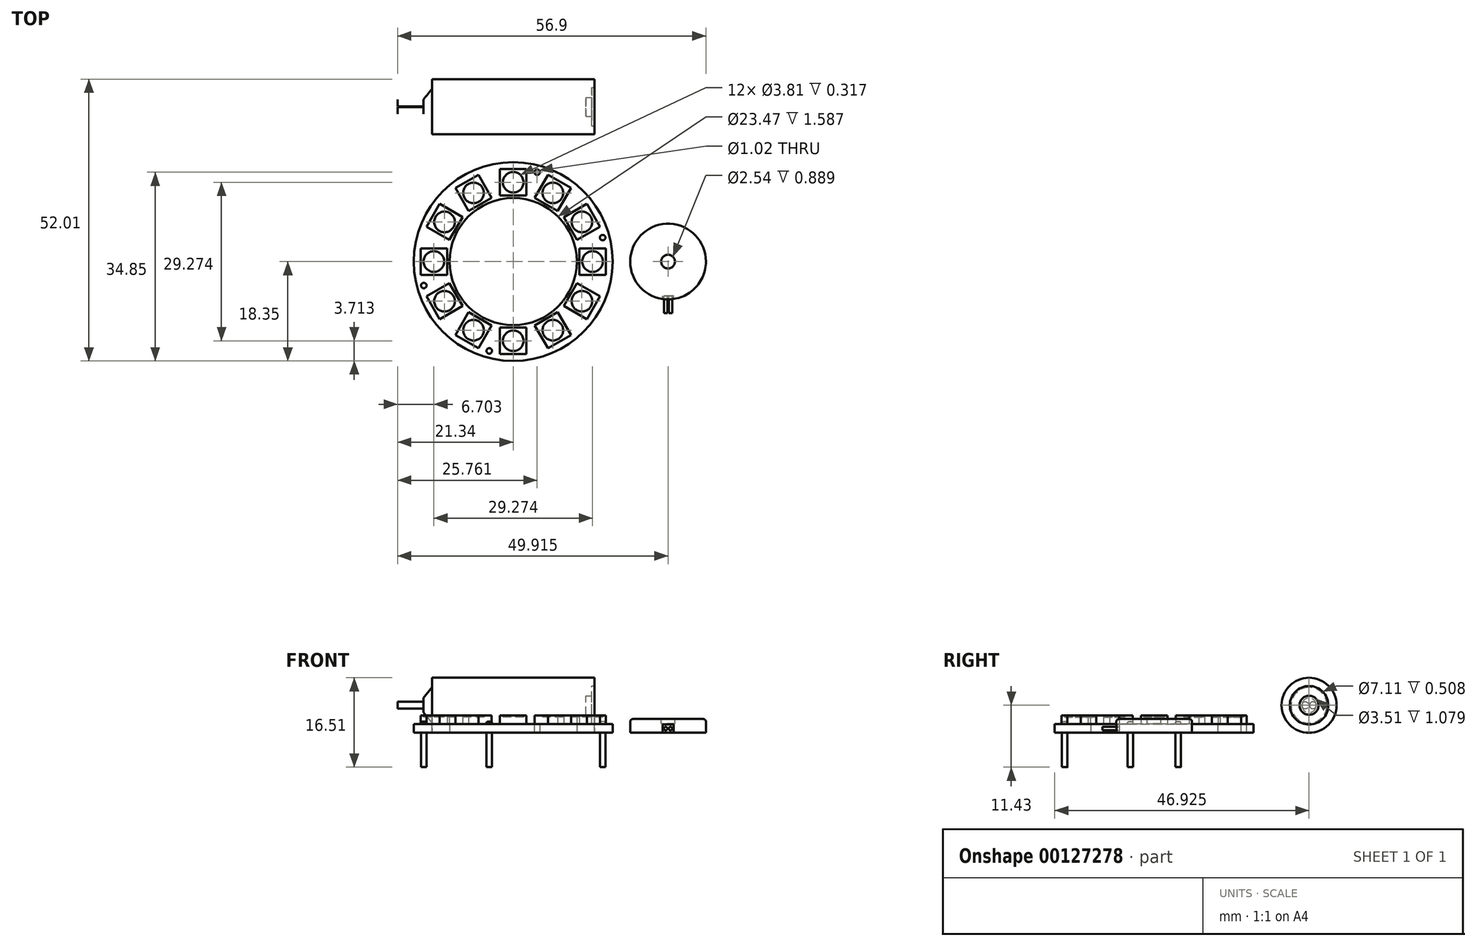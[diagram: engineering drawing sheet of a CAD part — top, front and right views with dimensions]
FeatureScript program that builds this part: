
annotation { "Feature Type Name" : "Feature", "Feature Type Description" : "" }
export const myFeature = defineFeature(function(context is Context, id is Id, definition is map)
    precondition{}
    {
        {
            var Q0;
            Q0=qCreatedBy(makeId("Top.planeOp"),FACE);
            var sketch = newSketch(context, id + "F0", { "sketchPlane" : qUnion([Q0])});
            skCircle(sketch, "E0", {"center": v(0, 0) * mm, "radius": 18.35 * mm});
            skCircle(sketch, "E1", {"center": v(0, 0) * mm, "radius": 11.73 * mm});
            skLineSegment(sketch, "E2", {"start": v(0, 0) * mm, "end": v(0, 18.35) * mm, "construction": true});
            skLineSegment(sketch, "E3.1.0", {"start": v(0, 0) * mm, "end": v(-4.75, 17.73) * mm, "construction": true});
            skLineSegment(sketch, "E3.2.0", {"start": v(0, 0) * mm, "end": v(-9.18, 15.9) * mm, "construction": true});
            skLineSegment(sketch, "E3.3.0", {"start": v(0, 0) * mm, "end": v(-12.98, 12.98) * mm, "construction": true});
            skLineSegment(sketch, "E3.4.0", {"start": v(0, 0) * mm, "end": v(-15.9, 9.18) * mm, "construction": true});
            skLineSegment(sketch, "E3.5.0", {"start": v(0, 0) * mm, "end": v(-17.73, 4.75) * mm, "construction": true});
            skLineSegment(sketch, "E3.6.0", {"start": v(0, 0) * mm, "end": v(-18.35, 0) * mm, "construction": true});
            skLineSegment(sketch, "E3.7.0", {"start": v(0, 0) * mm, "end": v(-17.73, -4.75) * mm, "construction": true});
            skLineSegment(sketch, "E3.8.0", {"start": v(0, 0) * mm, "end": v(-15.9, -9.18) * mm, "construction": true});
            skLineSegment(sketch, "E3.9.0", {"start": v(0, 0) * mm, "end": v(-12.98, -12.98) * mm, "construction": true});
            skLineSegment(sketch, "E3.10.0", {"start": v(0, 0) * mm, "end": v(-9.18, -15.9) * mm, "construction": true});
            skLineSegment(sketch, "E3.11.0", {"start": v(0, 0) * mm, "end": v(-4.75, -17.73) * mm, "construction": true});
            skLineSegment(sketch, "E3.12.0", {"start": v(0, 0) * mm, "end": v(0, -18.35) * mm, "construction": true});
            skLineSegment(sketch, "E3.13.0", {"start": v(0, 0) * mm, "end": v(4.75, -17.73) * mm, "construction": true});
            skLineSegment(sketch, "E3.14.0", {"start": v(0, 0) * mm, "end": v(9.18, -15.9) * mm, "construction": true});
            skLineSegment(sketch, "E3.15.0", {"start": v(0, 0) * mm, "end": v(12.98, -12.98) * mm, "construction": true});
            skLineSegment(sketch, "E3.16.0", {"start": v(0, 0) * mm, "end": v(15.9, -9.18) * mm, "construction": true});
            skLineSegment(sketch, "E3.17.0", {"start": v(0, 0) * mm, "end": v(17.73, -4.75) * mm, "construction": true});
            skLineSegment(sketch, "E3.18.0", {"start": v(0, 0) * mm, "end": v(18.35, 0) * mm, "construction": true});
            skLineSegment(sketch, "E3.19.0", {"start": v(0, 0) * mm, "end": v(17.73, 4.75) * mm, "construction": true});
            skLineSegment(sketch, "E3.20.0", {"start": v(0, 0) * mm, "end": v(15.9, 9.18) * mm, "construction": true});
            skLineSegment(sketch, "E3.21.0", {"start": v(0, 0) * mm, "end": v(12.98, 12.98) * mm, "construction": true});
            skLineSegment(sketch, "E3.22.0", {"start": v(0, 0) * mm, "end": v(9.18, 15.9) * mm, "construction": true});
            skLineSegment(sketch, "E3.23.0", {"start": v(0, 0) * mm, "end": v(4.75, 17.73) * mm, "construction": true});
            skCircle(sketch, "E4", {"center": v(4.42, 16.5) * mm, "radius": 0.5 * mm});
            skCircle(sketch, "E5", {"center": v(16.5, 4.42) * mm, "radius": 0.5 * mm});
            skCircle(sketch, "E6", {"center": v(-16.5, -4.42) * mm, "radius": 0.5 * mm});
            skCircle(sketch, "E7", {"center": v(-4.42, -16.5) * mm, "radius": 0.5 * mm});
            skSolve(sketch);
        }
        {
            var Q0;
            Q0=makeQuery(id+"F0.imprint","IMPRINT",FACE,{"disambiguationData":[TD([[makeQuery(id+"F0.imprint","IMPRINT",EDGE,{"derivedFrom":sQuery(id+"F0.wireOp",EDGE,"E0")}),1.0]])]});
            extrude(context, id + "F1", {"entities" : qUnion([Q0]), "depth" : 1.59 * mm});
        }
        {
            var Q0;
            Q0=makeQuery(id+"F1.opExtrude","CAP_FACE",FACE,{"disambiguationData":[OSD([sQuery(id+"F0.wireOp",EDGE,"E0"),sQuery(id+"F0.wireOp",EDGE,"E1"),sQuery(id+"F0.wireOp",EDGE,"E4"),sQuery(id+"F0.wireOp",EDGE,"E5"),sQuery(id+"F0.wireOp",EDGE,"E6"),sQuery(id+"F0.wireOp",EDGE,"E7")])],"isStart":false});
            var sketch = newSketch(context, id + "F2", { "sketchPlane" : qUnion([Q0])});
            skLineSegment(sketch, "E8.bottom", {"start": v(-2.44, 17.08) * mm, "end": v(2.44, 17.08) * mm});
            skLineSegment(sketch, "E8.top", {"start": v(-2.44, 12.2) * mm, "end": v(2.44, 12.2) * mm});
            skLineSegment(sketch, "E8.left", {"start": v(-2.44, 17.08) * mm, "end": v(-2.44, 12.2) * mm});
            skLineSegment(sketch, "E8.right", {"start": v(2.44, 17.08) * mm, "end": v(2.44, 12.2) * mm});
            skCircle(sketch, "E9", {"center": v(0, 14.64) * mm, "radius": 1.9 * mm});
            skPoint(sketch, "E9.centerSnap0", {"position": v(-2.44, 14.64) * mm});
            skCircle(sketch, "E10.1.0", {"center": v(-7.32, 12.68) * mm, "radius": 1.9 * mm});
            skLineSegment(sketch, "E10.1.1", {"start": v(-10.66, 13.57) * mm, "end": v(-6.42, 16.02) * mm});
            skLineSegment(sketch, "E10.1.2", {"start": v(-6.42, 16.02) * mm, "end": v(-3.98, 11.78) * mm});
            skLineSegment(sketch, "E10.1.3", {"start": v(-8.21, 9.34) * mm, "end": v(-3.98, 11.78) * mm});
            skLineSegment(sketch, "E10.1.4", {"start": v(-10.66, 13.57) * mm, "end": v(-8.21, 9.34) * mm});
            skCircle(sketch, "E10.2.0", {"center": v(-12.68, 7.32) * mm, "radius": 1.9 * mm});
            skLineSegment(sketch, "E10.2.1", {"start": v(-16.02, 6.42) * mm, "end": v(-13.57, 10.66) * mm});
            skLineSegment(sketch, "E10.2.2", {"start": v(-13.57, 10.66) * mm, "end": v(-9.34, 8.21) * mm});
            skLineSegment(sketch, "E10.2.3", {"start": v(-11.78, 3.98) * mm, "end": v(-9.34, 8.21) * mm});
            skLineSegment(sketch, "E10.2.4", {"start": v(-16.02, 6.42) * mm, "end": v(-11.78, 3.98) * mm});
            skCircle(sketch, "E10.3.0", {"center": v(-14.64, 0) * mm, "radius": 1.9 * mm});
            skLineSegment(sketch, "E10.3.1", {"start": v(-17.08, -2.44) * mm, "end": v(-17.08, 2.44) * mm});
            skLineSegment(sketch, "E10.3.2", {"start": v(-17.08, 2.44) * mm, "end": v(-12.2, 2.44) * mm});
            skLineSegment(sketch, "E10.3.3", {"start": v(-12.2, -2.44) * mm, "end": v(-12.2, 2.44) * mm});
            skLineSegment(sketch, "E10.3.4", {"start": v(-17.08, -2.44) * mm, "end": v(-12.2, -2.44) * mm});
            skCircle(sketch, "E10.4.0", {"center": v(-12.68, -7.32) * mm, "radius": 1.9 * mm});
            skLineSegment(sketch, "E10.4.1", {"start": v(-13.57, -10.66) * mm, "end": v(-16.02, -6.42) * mm});
            skLineSegment(sketch, "E10.4.2", {"start": v(-16.02, -6.42) * mm, "end": v(-11.78, -3.98) * mm});
            skLineSegment(sketch, "E10.4.3", {"start": v(-9.34, -8.21) * mm, "end": v(-11.78, -3.98) * mm});
            skLineSegment(sketch, "E10.4.4", {"start": v(-13.57, -10.66) * mm, "end": v(-9.34, -8.21) * mm});
            skCircle(sketch, "E10.5.0", {"center": v(-7.32, -12.68) * mm, "radius": 1.9 * mm});
            skLineSegment(sketch, "E10.5.1", {"start": v(-6.42, -16.02) * mm, "end": v(-10.66, -13.57) * mm});
            skLineSegment(sketch, "E10.5.2", {"start": v(-10.66, -13.57) * mm, "end": v(-8.21, -9.34) * mm});
            skLineSegment(sketch, "E10.5.3", {"start": v(-3.98, -11.78) * mm, "end": v(-8.21, -9.34) * mm});
            skLineSegment(sketch, "E10.5.4", {"start": v(-6.42, -16.02) * mm, "end": v(-3.98, -11.78) * mm});
            skCircle(sketch, "E10.6.0", {"center": v(0, -14.64) * mm, "radius": 1.9 * mm});
            skLineSegment(sketch, "E10.6.1", {"start": v(2.44, -17.08) * mm, "end": v(-2.44, -17.08) * mm});
            skLineSegment(sketch, "E10.6.2", {"start": v(-2.44, -17.08) * mm, "end": v(-2.44, -12.2) * mm});
            skLineSegment(sketch, "E10.6.3", {"start": v(2.44, -12.2) * mm, "end": v(-2.44, -12.2) * mm});
            skLineSegment(sketch, "E10.6.4", {"start": v(2.44, -17.08) * mm, "end": v(2.44, -12.2) * mm});
            skCircle(sketch, "E10.7.0", {"center": v(7.32, -12.68) * mm, "radius": 1.9 * mm});
            skLineSegment(sketch, "E10.7.1", {"start": v(10.66, -13.57) * mm, "end": v(6.42, -16.02) * mm});
            skLineSegment(sketch, "E10.7.2", {"start": v(6.42, -16.02) * mm, "end": v(3.98, -11.78) * mm});
            skLineSegment(sketch, "E10.7.3", {"start": v(8.21, -9.34) * mm, "end": v(3.98, -11.78) * mm});
            skLineSegment(sketch, "E10.7.4", {"start": v(10.66, -13.57) * mm, "end": v(8.21, -9.34) * mm});
            skCircle(sketch, "E10.8.0", {"center": v(12.68, -7.32) * mm, "radius": 1.9 * mm});
            skLineSegment(sketch, "E10.8.1", {"start": v(16.02, -6.42) * mm, "end": v(13.57, -10.66) * mm});
            skLineSegment(sketch, "E10.8.2", {"start": v(13.57, -10.66) * mm, "end": v(9.34, -8.21) * mm});
            skLineSegment(sketch, "E10.8.3", {"start": v(11.78, -3.98) * mm, "end": v(9.34, -8.21) * mm});
            skLineSegment(sketch, "E10.8.4", {"start": v(16.02, -6.42) * mm, "end": v(11.78, -3.98) * mm});
            skCircle(sketch, "E10.9.0", {"center": v(14.64, 0) * mm, "radius": 1.9 * mm});
            skLineSegment(sketch, "E10.9.1", {"start": v(17.08, 2.44) * mm, "end": v(17.08, -2.44) * mm});
            skLineSegment(sketch, "E10.9.2", {"start": v(17.08, -2.44) * mm, "end": v(12.2, -2.44) * mm});
            skLineSegment(sketch, "E10.9.3", {"start": v(12.2, 2.44) * mm, "end": v(12.2, -2.44) * mm});
            skLineSegment(sketch, "E10.9.4", {"start": v(17.08, 2.44) * mm, "end": v(12.2, 2.44) * mm});
            skCircle(sketch, "E10.10.0", {"center": v(12.68, 7.32) * mm, "radius": 1.9 * mm});
            skLineSegment(sketch, "E10.10.1", {"start": v(13.57, 10.66) * mm, "end": v(16.02, 6.42) * mm});
            skLineSegment(sketch, "E10.10.2", {"start": v(16.02, 6.42) * mm, "end": v(11.78, 3.98) * mm});
            skLineSegment(sketch, "E10.10.3", {"start": v(9.34, 8.21) * mm, "end": v(11.78, 3.98) * mm});
            skLineSegment(sketch, "E10.10.4", {"start": v(13.57, 10.66) * mm, "end": v(9.34, 8.21) * mm});
            skCircle(sketch, "E10.11.0", {"center": v(7.32, 12.68) * mm, "radius": 1.9 * mm});
            skLineSegment(sketch, "E10.11.1", {"start": v(6.42, 16.02) * mm, "end": v(10.66, 13.57) * mm});
            skLineSegment(sketch, "E10.11.2", {"start": v(10.66, 13.57) * mm, "end": v(8.21, 9.34) * mm});
            skLineSegment(sketch, "E10.11.3", {"start": v(3.98, 11.78) * mm, "end": v(8.21, 9.34) * mm});
            skLineSegment(sketch, "E10.11.4", {"start": v(6.42, 16.02) * mm, "end": v(3.98, 11.78) * mm});
            skPoint(sketch, "E10.center", {"position": v(0, 0) * mm});
            skSolve(sketch);
        }
        {
            var Q0;
            Q0=qSketchRegion(id+"F2",true);
            extrude(context, id + "F3", {"entities" : qUnion([Q0]), "operationType" : NewBodyOperationType.ADD, "depth" : 1.59 * mm});
        }
        {
            var Q0;
            Q0=makeQuery(id+"F3.boolean.opBoolean","SPLIT",FACE,{"disambiguationData":[TD([makeQuery(id+"F3.opExtrude","SWEPT_FACE",FACE,{"disambiguationData":[OSD([sQuery(id+"F2.wireOp",EDGE,"E9")])]})])],"derivedFrom":makeQuery(id+"F1.opExtrude","CAP_FACE",FACE,{"disambiguationData":[OSD([sQuery(id+"F0.wireOp",EDGE,"E0"),sQuery(id+"F0.wireOp",EDGE,"E1"),sQuery(id+"F0.wireOp",EDGE,"E4"),sQuery(id+"F0.wireOp",EDGE,"E5"),sQuery(id+"F0.wireOp",EDGE,"E6"),sQuery(id+"F0.wireOp",EDGE,"E7")])],"isStart":false})});
            var Q1;
            Q1=makeQuery(id+"F3.boolean.opBoolean","SPLIT",FACE,{"disambiguationData":[TD([makeQuery(id+"F3.opExtrude","SWEPT_FACE",FACE,{"disambiguationData":[OSD([sQuery(id+"F2.wireOp",EDGE,"E10.11.0")])]})])],"derivedFrom":makeQuery(id+"F1.opExtrude","CAP_FACE",FACE,{"disambiguationData":[OSD([sQuery(id+"F0.wireOp",EDGE,"E0"),sQuery(id+"F0.wireOp",EDGE,"E1"),sQuery(id+"F0.wireOp",EDGE,"E4"),sQuery(id+"F0.wireOp",EDGE,"E5"),sQuery(id+"F0.wireOp",EDGE,"E6"),sQuery(id+"F0.wireOp",EDGE,"E7")])],"isStart":false})});
            var Q2;
            Q2=makeQuery(id+"F3.boolean.opBoolean","SPLIT",FACE,{"disambiguationData":[TD([makeQuery(id+"F3.opExtrude","SWEPT_FACE",FACE,{"disambiguationData":[OSD([sQuery(id+"F2.wireOp",EDGE,"E10.10.0")])]})])],"derivedFrom":makeQuery(id+"F1.opExtrude","CAP_FACE",FACE,{"disambiguationData":[OSD([sQuery(id+"F0.wireOp",EDGE,"E0"),sQuery(id+"F0.wireOp",EDGE,"E1"),sQuery(id+"F0.wireOp",EDGE,"E4"),sQuery(id+"F0.wireOp",EDGE,"E5"),sQuery(id+"F0.wireOp",EDGE,"E6"),sQuery(id+"F0.wireOp",EDGE,"E7")])],"isStart":false})});
            var Q3;
            Q3=makeQuery(id+"F3.boolean.opBoolean","SPLIT",FACE,{"disambiguationData":[TD([makeQuery(id+"F3.opExtrude","SWEPT_FACE",FACE,{"disambiguationData":[OSD([sQuery(id+"F2.wireOp",EDGE,"E10.9.0")])]})])],"derivedFrom":makeQuery(id+"F1.opExtrude","CAP_FACE",FACE,{"disambiguationData":[OSD([sQuery(id+"F0.wireOp",EDGE,"E0"),sQuery(id+"F0.wireOp",EDGE,"E1"),sQuery(id+"F0.wireOp",EDGE,"E4"),sQuery(id+"F0.wireOp",EDGE,"E5"),sQuery(id+"F0.wireOp",EDGE,"E6"),sQuery(id+"F0.wireOp",EDGE,"E7")])],"isStart":false})});
            var Q4;
            Q4=makeQuery(id+"F3.boolean.opBoolean","SPLIT",FACE,{"disambiguationData":[TD([makeQuery(id+"F3.opExtrude","SWEPT_FACE",FACE,{"disambiguationData":[OSD([sQuery(id+"F2.wireOp",EDGE,"E10.8.0")])]})])],"derivedFrom":makeQuery(id+"F1.opExtrude","CAP_FACE",FACE,{"disambiguationData":[OSD([sQuery(id+"F0.wireOp",EDGE,"E0"),sQuery(id+"F0.wireOp",EDGE,"E1"),sQuery(id+"F0.wireOp",EDGE,"E4"),sQuery(id+"F0.wireOp",EDGE,"E5"),sQuery(id+"F0.wireOp",EDGE,"E6"),sQuery(id+"F0.wireOp",EDGE,"E7")])],"isStart":false})});
            var Q5;
            Q5=makeQuery(id+"F3.boolean.opBoolean","SPLIT",FACE,{"disambiguationData":[TD([makeQuery(id+"F3.opExtrude","SWEPT_FACE",FACE,{"disambiguationData":[OSD([sQuery(id+"F2.wireOp",EDGE,"E10.7.0")])]})])],"derivedFrom":makeQuery(id+"F1.opExtrude","CAP_FACE",FACE,{"disambiguationData":[OSD([sQuery(id+"F0.wireOp",EDGE,"E0"),sQuery(id+"F0.wireOp",EDGE,"E1"),sQuery(id+"F0.wireOp",EDGE,"E4"),sQuery(id+"F0.wireOp",EDGE,"E5"),sQuery(id+"F0.wireOp",EDGE,"E6"),sQuery(id+"F0.wireOp",EDGE,"E7")])],"isStart":false})});
            var Q6;
            Q6=makeQuery(id+"F3.boolean.opBoolean","SPLIT",FACE,{"disambiguationData":[TD([makeQuery(id+"F3.opExtrude","SWEPT_FACE",FACE,{"disambiguationData":[OSD([sQuery(id+"F2.wireOp",EDGE,"E10.6.0")])]})])],"derivedFrom":makeQuery(id+"F1.opExtrude","CAP_FACE",FACE,{"disambiguationData":[OSD([sQuery(id+"F0.wireOp",EDGE,"E0"),sQuery(id+"F0.wireOp",EDGE,"E1"),sQuery(id+"F0.wireOp",EDGE,"E4"),sQuery(id+"F0.wireOp",EDGE,"E5"),sQuery(id+"F0.wireOp",EDGE,"E6"),sQuery(id+"F0.wireOp",EDGE,"E7")])],"isStart":false})});
            var Q7;
            Q7=makeQuery(id+"F3.boolean.opBoolean","SPLIT",FACE,{"disambiguationData":[TD([makeQuery(id+"F3.opExtrude","SWEPT_FACE",FACE,{"disambiguationData":[OSD([sQuery(id+"F2.wireOp",EDGE,"E10.5.0")])]})])],"derivedFrom":makeQuery(id+"F1.opExtrude","CAP_FACE",FACE,{"disambiguationData":[OSD([sQuery(id+"F0.wireOp",EDGE,"E0"),sQuery(id+"F0.wireOp",EDGE,"E1"),sQuery(id+"F0.wireOp",EDGE,"E4"),sQuery(id+"F0.wireOp",EDGE,"E5"),sQuery(id+"F0.wireOp",EDGE,"E6"),sQuery(id+"F0.wireOp",EDGE,"E7")])],"isStart":false})});
            var Q8;
            Q8=makeQuery(id+"F3.boolean.opBoolean","SPLIT",FACE,{"disambiguationData":[TD([makeQuery(id+"F3.opExtrude","SWEPT_FACE",FACE,{"disambiguationData":[OSD([sQuery(id+"F2.wireOp",EDGE,"E10.4.0")])]})])],"derivedFrom":makeQuery(id+"F1.opExtrude","CAP_FACE",FACE,{"disambiguationData":[OSD([sQuery(id+"F0.wireOp",EDGE,"E0"),sQuery(id+"F0.wireOp",EDGE,"E1"),sQuery(id+"F0.wireOp",EDGE,"E4"),sQuery(id+"F0.wireOp",EDGE,"E5"),sQuery(id+"F0.wireOp",EDGE,"E6"),sQuery(id+"F0.wireOp",EDGE,"E7")])],"isStart":false})});
            var Q9;
            Q9=makeQuery(id+"F3.boolean.opBoolean","SPLIT",FACE,{"disambiguationData":[TD([makeQuery(id+"F3.opExtrude","SWEPT_FACE",FACE,{"disambiguationData":[OSD([sQuery(id+"F2.wireOp",EDGE,"E10.3.0")])]})])],"derivedFrom":makeQuery(id+"F1.opExtrude","CAP_FACE",FACE,{"disambiguationData":[OSD([sQuery(id+"F0.wireOp",EDGE,"E0"),sQuery(id+"F0.wireOp",EDGE,"E1"),sQuery(id+"F0.wireOp",EDGE,"E4"),sQuery(id+"F0.wireOp",EDGE,"E5"),sQuery(id+"F0.wireOp",EDGE,"E6"),sQuery(id+"F0.wireOp",EDGE,"E7")])],"isStart":false})});
            var Q10;
            Q10=makeQuery(id+"F3.boolean.opBoolean","SPLIT",FACE,{"disambiguationData":[TD([makeQuery(id+"F3.opExtrude","SWEPT_FACE",FACE,{"disambiguationData":[OSD([sQuery(id+"F2.wireOp",EDGE,"E10.2.0")])]})])],"derivedFrom":makeQuery(id+"F1.opExtrude","CAP_FACE",FACE,{"disambiguationData":[OSD([sQuery(id+"F0.wireOp",EDGE,"E0"),sQuery(id+"F0.wireOp",EDGE,"E1"),sQuery(id+"F0.wireOp",EDGE,"E4"),sQuery(id+"F0.wireOp",EDGE,"E5"),sQuery(id+"F0.wireOp",EDGE,"E6"),sQuery(id+"F0.wireOp",EDGE,"E7")])],"isStart":false})});
            var Q11;
            Q11=makeQuery(id+"F3.boolean.opBoolean","SPLIT",FACE,{"disambiguationData":[TD([makeQuery(id+"F3.opExtrude","SWEPT_FACE",FACE,{"disambiguationData":[OSD([sQuery(id+"F2.wireOp",EDGE,"E10.1.0")])]})])],"derivedFrom":makeQuery(id+"F1.opExtrude","CAP_FACE",FACE,{"disambiguationData":[OSD([sQuery(id+"F0.wireOp",EDGE,"E0"),sQuery(id+"F0.wireOp",EDGE,"E1"),sQuery(id+"F0.wireOp",EDGE,"E4"),sQuery(id+"F0.wireOp",EDGE,"E5"),sQuery(id+"F0.wireOp",EDGE,"E6"),sQuery(id+"F0.wireOp",EDGE,"E7")])],"isStart":false})});
            extrude(context, id + "F4", {"entities" : qUnion([Q0, Q1, Q2, Q3, Q4, Q5, Q6, Q7, Q8, Q9, Q10, Q11]), "operationType" : NewBodyOperationType.ADD, "depth" : 1.27 * mm});
        }
        {
            var Q0;
            Q0=makeQuery(id+"F0.imprint","IMPRINT",FACE,{"disambiguationData":[TD([[makeQuery(id+"F0.imprint","IMPRINT",EDGE,{"derivedFrom":sQuery(id+"F0.wireOp",EDGE,"E7")}),1.0]])]});
            var Q1;
            Q1=makeQuery(id+"F0.imprint","IMPRINT",FACE,{"disambiguationData":[TD([[makeQuery(id+"F0.imprint","IMPRINT",EDGE,{"derivedFrom":sQuery(id+"F0.wireOp",EDGE,"E6")}),1.0]])]});
            var Q2;
            Q2=makeQuery(id+"F0.imprint","IMPRINT",FACE,{"disambiguationData":[TD([[makeQuery(id+"F0.imprint","IMPRINT",EDGE,{"derivedFrom":sQuery(id+"F0.wireOp",EDGE,"E5")}),1.0]])]});
            extrude(context, id + "F5", {"entities" : qUnion([Q0, Q1, Q2]), "operationType" : NewBodyOperationType.ADD, "oppositeDirection" : true, "depth" : 6.35 * mm, "hasSecondDirection" : true, "secondDirectionOppositeDirection" : false, "secondDirectionDepth" : 2.03 * mm});
        }
        {
            var Q0;
            Q0=makeQuery(id+"F1.opExtrude","CAP_EDGE",EDGE,{"disambiguationData":[OSD([sQuery(id+"F0.wireOp",EDGE,"E5")])],"isStart":false});
            var Q1;
            Q1=makeQuery(id+"F5.opExtrude","CAP_EDGE",EDGE,{"disambiguationData":[OSD([sQuery(id+"F0.wireOp",EDGE,"E5")])],"isStart":true});
            var Q2;
            Q2=makeQuery(id+"F5.opExtrude","CAP_EDGE",EDGE,{"disambiguationData":[OSD([sQuery(id+"F0.wireOp",EDGE,"E6")])],"isStart":true});
            var Q3;
            Q3=makeQuery(id+"F5.opExtrude","CAP_EDGE",EDGE,{"disambiguationData":[OSD([sQuery(id+"F0.wireOp",EDGE,"E7")])],"isStart":true});
            var Q4;
            Q4=makeQuery(id+"F1.opExtrude","CAP_EDGE",EDGE,{"disambiguationData":[OSD([sQuery(id+"F0.wireOp",EDGE,"E6")])],"isStart":false});
            var Q5;
            Q5=makeQuery(id+"F1.opExtrude","CAP_EDGE",EDGE,{"disambiguationData":[OSD([sQuery(id+"F0.wireOp",EDGE,"E7")])],"isStart":false});
            fillet(context, id + "F6", {"entities" : qUnion([Q0, Q1, Q2, Q3, Q4, Q5]), "radius" : 0.2 * mm, "tangentPropagation" : true, "allowEdgeOverflow" : false});
        }
        {
            var Q0;
            Q0=qCreatedBy(makeId("Top.planeOp"),FACE);
            var sketch = newSketch(context, id + "F7", { "sketchPlane" : qUnion([Q0])});
            skCircle(sketch, "E11", {"center": v(28.58, 0) * mm, "radius": 6.99 * mm});
            skSolve(sketch);
        }
        {
            var Q0;
            Q0=makeQuery(id+"F7.imprint","IMPRINT",FACE,{"disambiguationData":[TD([[makeQuery(id+"F7.imprint","IMPRINT",EDGE,{"derivedFrom":sQuery(id+"F7.wireOp",EDGE,"E11")}),1.0]])]});
            extrude(context, id + "F8", {"entities" : qUnion([Q0]), "depth" : 2.54 * mm});
        }
        {
            var Q0;
            Q0=makeQuery(id+"F8.opExtrude","CAP_EDGE",EDGE,{"disambiguationData":[OSD([sQuery(id+"F7.wireOp",EDGE,"E11")])],"isStart":false});
            fillet(context, id + "F9", {"entities" : qUnion([Q0]), "radius" : 0.5 * mm, "tangentPropagation" : true, "allowEdgeOverflow" : false});
        }
        {
            var Q0;
            Q0=makeQuery(id+"F8.opExtrude","CAP_FACE",FACE,{"disambiguationData":[OSD([sQuery(id+"F7.wireOp",EDGE,"E11")])],"isStart":false});
            var sketch = newSketch(context, id + "F10", { "sketchPlane" : qUnion([Q0])});
            skCircle(sketch, "E12", {"center": v(28.58, 0) * mm, "radius": 1.27 * mm});
            skSolve(sketch);
        }
        {
            var Q0;
            Q0=makeQuery(id+"F10.imprint","IMPRINT",FACE,{"disambiguationData":[TD([[makeQuery(id+"F10.imprint","IMPRINT",EDGE,{"derivedFrom":sQuery(id+"F10.wireOp",EDGE,"E12")}),1.0]])]});
            extrude(context, id + "F11", {"entities" : qUnion([Q0]), "operationType" : NewBodyOperationType.REMOVE, "oppositeDirection" : true, "depth" : 0.89 * mm});
        }
        {
            var Q0;
            Q0=qCreatedBy(makeId("Front.planeOp"),FACE);
            var sketch = newSketch(context, id + "F12", { "sketchPlane" : qUnion([Q0])});
            skLineSegment(sketch, "E13", {"start": v(27.56, 0) * mm, "end": v(27.56, 1.52) * mm});
            skLineSegment(sketch, "E14", {"start": v(27.56, 1.52) * mm, "end": v(29.6, 1.52) * mm});
            skLineSegment(sketch, "E15", {"start": v(29.6, 1.52) * mm, "end": v(29.6, 0) * mm});
            skLineSegment(sketch, "E16", {"start": v(29.6, 0) * mm, "end": v(27.56, 0) * mm});
            skLineSegment(sketch, "E17.0", {"start": v(21.59, 0) * mm, "end": v(35.56, 0) * mm, "construction": true});
            skPoint(sketch, "E18", {"position": v(28.58, 0) * mm});
            skSolve(sketch);
        }
        {
            var Q0;
            Q0 = qSketchRegion(id + "F12", true);
            extrude(context, id + "F13", {"entities" : qUnion([Q0]), "operationType" : NewBodyOperationType.REMOVE, "depth" : 7.62 * mm, "hasSecondDirection" : true, "secondDirectionOppositeDirection" : false, "secondDirectionDepth" : 6.35 * mm});
        }
        {
            var Q0;
            Q0=makeQuery(id+"F13.boolean.opBoolean","COPY",FACE,{"derivedFrom":makeQuery(id+"F13.opExtrude","CAP_FACE",FACE,{"disambiguationData":[OSD([sQuery(id+"F12.wireOp",EDGE,"E13"),sQuery(id+"F12.wireOp",EDGE,"E14"),sQuery(id+"F12.wireOp",EDGE,"E15"),sQuery(id+"F12.wireOp",EDGE,"E16")])],"isStart":true})});
            var sketch = newSketch(context, id + "F14", { "sketchPlane" : qUnion([Q0])});
            skCircle(sketch, "E19", {"center": v(28.13, 0.76) * mm, "radius": 0.32 * mm});
            skPoint(sketch, "E19.centerSnap0", {"position": v(27.56, 0.76) * mm});
            skCircle(sketch, "E20", {"center": v(29.02, 0.76) * mm, "radius": 0.32 * mm});
            skLineSegment(sketch, "E21", {"start": v(28.13, 0.76) * mm, "end": v(29.02, 0.76) * mm, "construction": true});
            skLineSegment(sketch, "E22", {"start": v(28.58, 0.76) * mm, "end": v(28.58, 1.52) * mm, "construction": true});
            skSolve(sketch);
        }
        {
            var Q0;
            Q0=makeQuery(id+"F14.imprint","IMPRINT",FACE,{"disambiguationData":[TD([[makeQuery(id+"F14.imprint","IMPRINT",EDGE,{"derivedFrom":sQuery(id+"F14.wireOp",EDGE,"E19")}),1.0]])]});
            var Q1;
            Q1=makeQuery(id+"F14.imprint","IMPRINT",FACE,{"disambiguationData":[TD([[makeQuery(id+"F14.imprint","IMPRINT",EDGE,{"derivedFrom":sQuery(id+"F14.wireOp",EDGE,"E20")}),1.0]])]});
            extrude(context, id + "F15", {"entities" : qUnion([Q0, Q1]), "operationType" : NewBodyOperationType.ADD, "depth" : 3.17 * mm});
        }
        {
            var Q0;
            Q0=qCreatedBy(makeId("Right.planeOp"),FACE);
            var sketch = newSketch(context, id + "F16", { "sketchPlane" : qUnion([Q0])});
            skCircle(sketch, "E23", {"center": v(28.58, 5.08) * mm, "radius": 5.08 * mm});
            skLineSegment(sketch, "E24", {"start": v(0, 0) * mm, "end": v(28.57, 0) * mm, "construction": true});
            skSolve(sketch);
        }
        {
            var Q0;
            Q0=makeQuery(id+"F16.imprint","IMPRINT",FACE,{"disambiguationData":[TD([[makeQuery(id+"F16.imprint","IMPRINT",EDGE,{"derivedFrom":sQuery(id+"F16.wireOp",EDGE,"E23")}),1.0]])]});
            extrude(context, id + "F17", {"entities" : qUnion([Q0]), "endBound" : BoundingType.SYMMETRIC, "depth" : 29.97 * mm});
        }
        {
            var Q0;
            Q0=makeQuery(id+"F17.opExtrude","CAP_FACE",FACE,{"disambiguationData":[OSD([sQuery(id+"F16.wireOp",EDGE,"E23")])],"isStart":false});
            var sketch = newSketch(context, id + "F18", { "sketchPlane" : qUnion([Q0])});
            skCircle(sketch, "E25", {"center": v(28.58, 5.08) * mm, "radius": 1.75 * mm});
            skCircle(sketch, "E26", {"center": v(28.58, 5.08) * mm, "radius": 3.56 * mm});
            skSolve(sketch);
        }
        {
            var Q0;
            Q0=makeQuery(id+"F18.imprint","IMPRINT",FACE,{"disambiguationData":[TD([[makeQuery(id+"F18.imprint","IMPRINT",EDGE,{"derivedFrom":sQuery(id+"F18.wireOp",EDGE,"E25")}),1.0]])]});
            extrude(context, id + "F19", {"entities" : qUnion([Q0]), "operationType" : NewBodyOperationType.REMOVE, "oppositeDirection" : true, "depth" : 1.59 * mm});
        }
        {
            var Q0;
            Q0=makeQuery(id+"F18.imprint","IMPRINT",FACE,{"disambiguationData":[TD([[makeQuery(id+"F18.imprint","IMPRINT",EDGE,{"derivedFrom":sQuery(id+"F18.wireOp",EDGE,"E25")}),-1.0]])]});
            extrude(context, id + "F20", {"entities" : qUnion([Q0]), "operationType" : NewBodyOperationType.REMOVE, "oppositeDirection" : true, "depth" : 0.5 * mm});
        }
        {
            var Q0;
            Q0=makeQuery(id+"F17.opExtrude","CAP_FACE",FACE,{"disambiguationData":[OSD([sQuery(id+"F16.wireOp",EDGE,"E23")])],"isStart":true});
            var sketch = newSketch(context, id + "F21", { "sketchPlane" : qUnion([Q0])});
            skCircle(sketch, "E27.0", {"center": v(-28.58, 5.08) * mm, "radius": 5.08 * mm, "construction": true});
            skCircle(sketch, "E28", {"center": v(-27.88, 5.08) * mm, "radius": 0.64 * mm});
            skCircle(sketch, "E29", {"center": v(-29.27, 5.08) * mm, "radius": 0.64 * mm});
            skLineSegment(sketch, "E30", {"start": v(-29.27, 5.08) * mm, "end": v(-27.88, 5.08) * mm, "construction": true});
            skSolve(sketch);
        }
        {
            var Q0;
            Q0=makeQuery(id+"F21.imprint","IMPRINT",FACE,{"disambiguationData":[TD([[makeQuery(id+"F21.imprint","IMPRINT",EDGE,{"derivedFrom":sQuery(id+"F21.wireOp",EDGE,"E29")}),1.0]])]});
            var Q1;
            Q1=makeQuery(id+"F21.imprint","IMPRINT",FACE,{"disambiguationData":[TD([[makeQuery(id+"F21.imprint","IMPRINT",EDGE,{"derivedFrom":sQuery(id+"F21.wireOp",EDGE,"E28")}),1.0]])]});
            extrude(context, id + "F22", {"entities" : qUnion([Q0, Q1]), "operationType" : NewBodyOperationType.ADD, "depth" : 6.35 * mm});
        }
        {
            var Q0;
            Q0=qCreatedBy(makeId("Top.planeOp"),FACE);
            cPlane(context, id + "F23", {"entities" : qUnion([Q0]), "cplaneType" : CPlaneType.OFFSET, "offset" : 5.08 * mm, "width" : 152.4 * mm, "height" : 152.4 * mm});
        }
        {
            var Q0;
            Q0=qCreatedBy(id+"F23.planeOp",FACE);
            var sketch = newSketch(context, id + "F24", { "sketchPlane" : qUnion([Q0])});
            skLineSegment(sketch, "E31", {"start": v(-16.57, 28.58) * mm, "end": v(-16.57, 29.9) * mm});
            skLineSegment(sketch, "E32.0", {"start": v(-14.99, 33.66) * mm, "end": v(-14.99, 23.5) * mm});
            skLineSegment(sketch, "E33", {"start": v(-16.57, 29.9) * mm, "end": v(-14.99, 31.88) * mm});
            skLineSegment(sketch, "E34", {"start": v(-16.57, 28.58) * mm, "end": v(-14.99, 28.58) * mm});
            skSolve(sketch);
        }
        {
            var Q0;
            Q0=makeQuery(id+"F24.imprint","IMPRINT",FACE,{"disambiguationData":[TD([[makeQuery(id+"F24.imprint","IMPRINT",EDGE,{"derivedFrom":sQuery(id+"F24.wireOp",EDGE,"E31")}),-1.0]])]});
            var Q1;
            Q1=sQuery(id+"F24.wireOp",EDGE,"E34");
            revolve(context, id + "F25", {"operationType" : NewBodyOperationType.ADD, "entities" : qUnion([Q0]), "axis" : qUnion([Q1]), "revolveType" : RevolveType.FULL});
        }
    });
